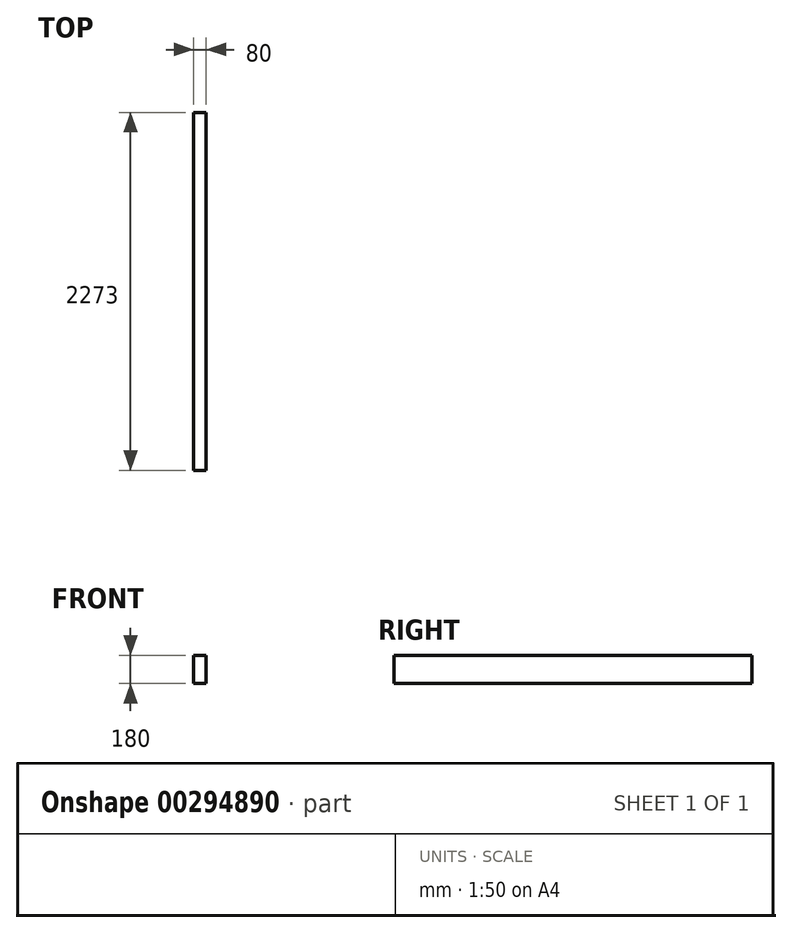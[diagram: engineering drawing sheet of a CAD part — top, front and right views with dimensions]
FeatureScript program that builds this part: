
annotation { "Feature Type Name" : "Feature", "Feature Type Description" : "" }
export const myFeature = defineFeature(function(context is Context, id is Id, definition is map)
    precondition{}
    {
        {
            var Q0;
            Q0=qCreatedBy(makeId("Front.planeOp"),FACE);
            var sketch = newSketch(context, id + "F0", { "sketchPlane" : qUnion([Q0])});
            skLineSegment(sketch, "E0.bottom", {"start": v(40, 90) * mm, "end": v(-40, 90) * mm});
            skLineSegment(sketch, "E0.top", {"start": v(40, -90) * mm, "end": v(-40, -90) * mm});
            skLineSegment(sketch, "E0.left", {"start": v(40, 90) * mm, "end": v(40, -90) * mm});
            skLineSegment(sketch, "E0.right", {"start": v(-40, 90) * mm, "end": v(-40, -90) * mm});
            skPoint(sketch, "E0.middle", {"position": v(0, 0) * mm});
            skSolve(sketch);
        }
        {
            var Q0;
            Q0=makeQuery(id+"F0.imprint","IMPRINT",FACE,{"disambiguationData":[TD([[makeQuery(id+"F0.imprint","IMPRINT",EDGE,{"derivedFrom":sQuery(id+"F0.wireOp",EDGE,"E0.bottom")}),1.0]])]});
            extrude(context, id + "F1", {"entities" : qUnion([Q0]), "depth" : (2200 - 47 + 120) * mm});
        }
    });
